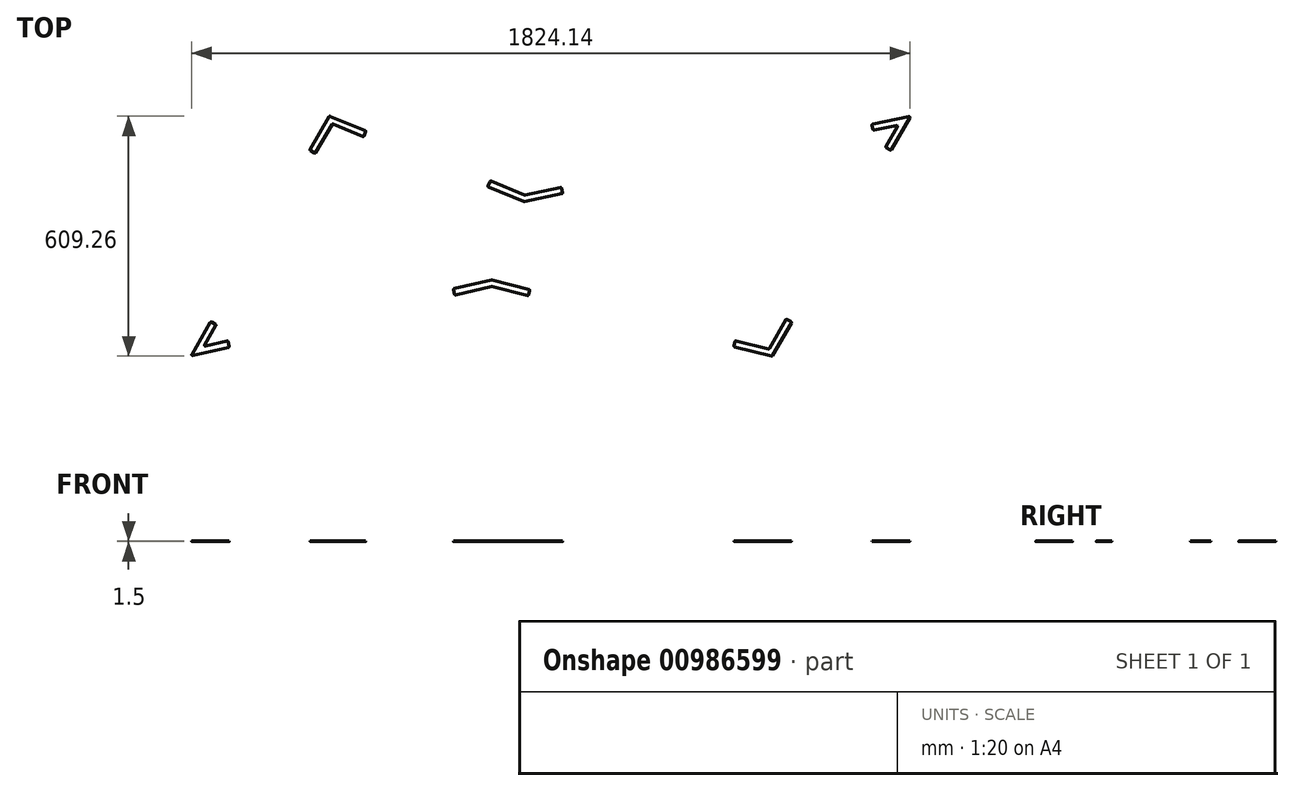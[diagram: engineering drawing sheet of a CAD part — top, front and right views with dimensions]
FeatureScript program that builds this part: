
annotation { "Feature Type Name" : "Feature", "Feature Type Description" : "" }
export const myFeature = defineFeature(function(context is Context, id is Id, definition is map)
    precondition{}
    {
        {
            var Q0;
            Q0=qCreatedBy(makeId("Top.planeOp"),FACE);
            var sketch = newSketch(context, id + "F0", { "sketchPlane" : qUnion([Q0])});
            skLineSegment(sketch, "E0", {"start": v(0, 0) * mm, "end": v(355, 614.88) * mm});
            skLineSegment(sketch, "E1", {"start": v(355, 614.88) * mm, "end": v(851.97, 414.09) * mm});
            skLineSegment(sketch, "E2", {"start": v(355, 614.88) * mm, "end": v(806.95, 614.88) * mm, "construction": true});
            skLineSegment(sketch, "E3", {"start": v(851.97, 414.09) * mm, "end": v(1836.1, 614.88) * mm});
            skLineSegment(sketch, "E4", {"start": v(851.97, 414.09) * mm, "end": v(1531.4, 414.09) * mm, "construction": true});
            skLineSegment(sketch, "E5", {"start": v(1836.1, 614.88) * mm, "end": v(1481.1, 0) * mm});
            skLineSegment(sketch, "E6", {"start": v(1481.1, 0) * mm, "end": v(767.8, 177.26) * mm});
            skLineSegment(sketch, "E7", {"start": v(767.8, 177.26) * mm, "end": v(0, 0) * mm});
            skLineSegment(sketch, "E8.0", {"start": v(767.98, 197.83) * mm, "end": v(40.32, 29.83) * mm});
            skLineSegment(sketch, "E8.1", {"start": v(363.63, 589.82) * mm, "end": v(850.06, 393.29) * mm});
            skLineSegment(sketch, "E8.2", {"start": v(850.06, 393.29) * mm, "end": v(1796.57, 586.4) * mm});
            skLineSegment(sketch, "E8.3", {"start": v(40.32, 29.83) * mm, "end": v(363.63, 589.82) * mm});
            skLineSegment(sketch, "E8.4", {"start": v(1796.57, 586.4) * mm, "end": v(1471.32, 23.04) * mm});
            skLineSegment(sketch, "E8.5", {"start": v(1471.32, 23.04) * mm, "end": v(767.98, 197.83) * mm});
            skLineSegment(sketch, "E9", {"start": v(0, 0) * mm, "end": v(40.32, 29.83) * mm});
            skLineSegment(sketch, "E10", {"start": v(363.63, 589.82) * mm, "end": v(355, 614.88) * mm});
            skLineSegment(sketch, "E11", {"start": v(850.06, 393.29) * mm, "end": v(851.97, 414.09) * mm});
            skLineSegment(sketch, "E12", {"start": v(767.98, 197.83) * mm, "end": v(767.8, 177.26) * mm});
            skLineSegment(sketch, "E13", {"start": v(1471.32, 23.04) * mm, "end": v(1481.1, 0) * mm});
            skLineSegment(sketch, "E14", {"start": v(1796.57, 586.4) * mm, "end": v(1836.1, 614.88) * mm});
            skSolve(sketch);
        }
        {
            var Q0;
            Q0=qCreatedBy(makeId("Top.planeOp"),FACE);
            var sketch = newSketch(context, id + "F1", { "sketchPlane" : qUnion([Q0])});
            skLineSegment(sketch, "E15.0", {"start": v(767.82, 179.32) * mm, "end": v(674.12, 157.69) * mm});
            skLineSegment(sketch, "E15.1", {"start": v(355.86, 612.37) * mm, "end": v(448.58, 574.91) * mm});
            skLineSegment(sketch, "E15.2", {"start": v(851.78, 412) * mm, "end": v(945.04, 431.04) * mm});
            skLineSegment(sketch, "E15.3", {"start": v(4.03, 2.98) * mm, "end": v(54.03, 89.59) * mm});
            skLineSegment(sketch, "E15.4", {"start": v(1832.15, 612.03) * mm, "end": v(1782.15, 525.43) * mm});
            skLineSegment(sketch, "E15.5", {"start": v(1480.13, 2.3) * mm, "end": v(1383.08, 26.42) * mm});
            skLineSegment(sketch, "E16.0", {"start": v(767.96, 195.77) * mm, "end": v(670.52, 173.28) * mm});
            skLineSegment(sketch, "E16.1", {"start": v(362.76, 592.33) * mm, "end": v(442.59, 560.08) * mm});
            skLineSegment(sketch, "E16.2", {"start": v(850.26, 395.37) * mm, "end": v(948.24, 415.36) * mm});
            skLineSegment(sketch, "E16.3", {"start": v(36.29, 26.85) * mm, "end": v(67.89, 81.59) * mm});
            skLineSegment(sketch, "E16.4", {"start": v(1800.53, 589.25) * mm, "end": v(1768.3, 533.43) * mm});
            skLineSegment(sketch, "E16.5", {"start": v(1472.3, 20.74) * mm, "end": v(1386.94, 41.95) * mm});
            skLineSegment(sketch, "E17", {"start": v(67.89, 81.59) * mm, "end": v(54.03, 89.59) * mm});
            skLineSegment(sketch, "E18", {"start": v(97.87, 41.07) * mm, "end": v(101.47, 25.48) * mm});
            skLineSegment(sketch, "E19", {"start": v(319.72, 517.77) * mm, "end": v(305.86, 525.77) * mm});
            skLineSegment(sketch, "E20", {"start": v(442.59, 560.08) * mm, "end": v(448.58, 574.91) * mm});
            skLineSegment(sketch, "E21", {"start": v(758.1, 432.6) * mm, "end": v(764.09, 447.44) * mm});
            skLineSegment(sketch, "E22", {"start": v(948.24, 415.36) * mm, "end": v(945.04, 431.04) * mm});
            skLineSegment(sketch, "E23", {"start": v(1734.17, 592.04) * mm, "end": v(1737.37, 576.36) * mm});
            skLineSegment(sketch, "E24", {"start": v(1768.3, 533.43) * mm, "end": v(1782.15, 525.43) * mm});
            skLineSegment(sketch, "E25", {"start": v(1516.27, 96.9) * mm, "end": v(1530.13, 88.9) * mm});
            skLineSegment(sketch, "E26", {"start": v(1386.94, 41.95) * mm, "end": v(1383.08, 26.42) * mm});
            skLineSegment(sketch, "E27", {"start": v(670.52, 173.28) * mm, "end": v(674.12, 157.69) * mm});
            skLineSegment(sketch, "E28", {"start": v(861.15, 156.13) * mm, "end": v(865, 171.65) * mm});
            skLineSegment(sketch, "E29.trimOffspring", {"start": v(319.72, 517.77) * mm, "end": v(362.76, 592.33) * mm});
            skLineSegment(sketch, "E30.trimOffspring", {"start": v(305.86, 525.77) * mm, "end": v(355.86, 612.37) * mm});
            skLineSegment(sketch, "E31.trimOffspring", {"start": v(758.1, 432.6) * mm, "end": v(850.26, 395.37) * mm});
            skLineSegment(sketch, "E32.trimOffspring", {"start": v(764.09, 447.44) * mm, "end": v(851.78, 412) * mm});
            skLineSegment(sketch, "E33.trimOffspring", {"start": v(1737.37, 576.36) * mm, "end": v(1800.53, 589.25) * mm});
            skLineSegment(sketch, "E34.trimOffspring", {"start": v(1734.17, 592.04) * mm, "end": v(1832.15, 612.03) * mm});
            skLineSegment(sketch, "E35.trimOffspring", {"start": v(1516.27, 96.9) * mm, "end": v(1472.3, 20.74) * mm});
            skLineSegment(sketch, "E36.trimOffspring", {"start": v(1530.13, 88.9) * mm, "end": v(1480.13, 2.3) * mm});
            skLineSegment(sketch, "E37.trimOffspring", {"start": v(865, 171.65) * mm, "end": v(767.96, 195.77) * mm});
            skLineSegment(sketch, "E38.trimOffspring", {"start": v(861.15, 156.13) * mm, "end": v(767.82, 179.32) * mm});
            skLineSegment(sketch, "E39.trimOffspring", {"start": v(101.47, 25.48) * mm, "end": v(4.03, 2.98) * mm});
            skLineSegment(sketch, "E40.trimOffspring", {"start": v(97.87, 41.07) * mm, "end": v(36.29, 26.85) * mm});
            skSolve(sketch);
        }
        {
            var Q0;
            Q0 = qSketchRegion(id + "F1", true);
            extrude(context, id + "F2", {"entities" : qUnion([Q0]), "oppositeDirection" : true, "depth" : 1.5 * mm, "offsetDistance" : 25 * mm});
        }
        {
            var Q0;
            Q0=makeQuery(id+"F2.opExtrude","SWEPT_EDGE",EDGE,{"disambiguationData":[OSD([sQuery(id+"F1.wireOp",EDGE,"E15.1"),sQuery(id+"F1.wireOp",EDGE,"E30.trimOffspring")])]});
            var Q1;
            Q1=makeQuery(id+"F2.opExtrude","SWEPT_EDGE",EDGE,{"disambiguationData":[OSD([sQuery(id+"F1.wireOp",EDGE,"E15.1"),sQuery(id+"F1.wireOp",EDGE,"E20")])]});
            var Q2;
            Q2=makeQuery(id+"F2.opExtrude","SWEPT_EDGE",EDGE,{"disambiguationData":[OSD([sQuery(id+"F1.wireOp",EDGE,"E16.1"),sQuery(id+"F1.wireOp",EDGE,"E20")])]});
            var Q3;
            Q3=makeQuery(id+"F2.opExtrude","SWEPT_EDGE",EDGE,{"disambiguationData":[OSD([sQuery(id+"F1.wireOp",EDGE,"E16.1"),sQuery(id+"F1.wireOp",EDGE,"E29.trimOffspring")])]});
            var Q4;
            Q4=makeQuery(id+"F2.opExtrude","SWEPT_EDGE",EDGE,{"disambiguationData":[OSD([sQuery(id+"F1.wireOp",EDGE,"E19"),sQuery(id+"F1.wireOp",EDGE,"E29.trimOffspring")])]});
            var Q5;
            Q5=makeQuery(id+"F2.opExtrude","SWEPT_EDGE",EDGE,{"disambiguationData":[OSD([sQuery(id+"F1.wireOp",EDGE,"E19"),sQuery(id+"F1.wireOp",EDGE,"E30.trimOffspring")])]});
            fillet(context, id + "F3", {"entities" : qUnion([Q0, Q1, Q2, Q3, Q4, Q5]), "radius" : 2 * mm, "tangentPropagation" : true, "allowEdgeOverflow" : false});
        }
        {
            var Q0;
            Q0=makeQuery(id+"F2.opExtrude","SWEPT_EDGE",EDGE,{"disambiguationData":[OSD([sQuery(id+"F1.wireOp",EDGE,"E21"),sQuery(id+"F1.wireOp",EDGE,"E32.trimOffspring")])]});
            var Q1;
            Q1=makeQuery(id+"F2.opExtrude","SWEPT_EDGE",EDGE,{"disambiguationData":[OSD([sQuery(id+"F1.wireOp",EDGE,"E21"),sQuery(id+"F1.wireOp",EDGE,"E31.trimOffspring")])]});
            var Q2;
            Q2=makeQuery(id+"F2.opExtrude","SWEPT_EDGE",EDGE,{"disambiguationData":[OSD([sQuery(id+"F1.wireOp",EDGE,"E15.2"),sQuery(id+"F1.wireOp",EDGE,"E32.trimOffspring")])]});
            var Q3;
            Q3=makeQuery(id+"F2.opExtrude","SWEPT_EDGE",EDGE,{"disambiguationData":[OSD([sQuery(id+"F1.wireOp",EDGE,"E15.2"),sQuery(id+"F1.wireOp",EDGE,"E22")])]});
            var Q4;
            Q4=makeQuery(id+"F2.opExtrude","SWEPT_EDGE",EDGE,{"disambiguationData":[OSD([sQuery(id+"F1.wireOp",EDGE,"E16.2"),sQuery(id+"F1.wireOp",EDGE,"E22")])]});
            var Q5;
            Q5=makeQuery(id+"F2.opExtrude","SWEPT_EDGE",EDGE,{"disambiguationData":[OSD([sQuery(id+"F1.wireOp",EDGE,"E16.2"),sQuery(id+"F1.wireOp",EDGE,"E31.trimOffspring")])]});
            fillet(context, id + "F4", {"entities" : qUnion([Q0, Q1, Q2, Q3, Q4, Q5]), "radius" : 2 * mm, "tangentPropagation" : true, "allowEdgeOverflow" : false});
        }
        {
            var Q0;
            Q0=makeQuery(id+"F2.opExtrude","SWEPT_EDGE",EDGE,{"disambiguationData":[OSD([sQuery(id+"F1.wireOp",EDGE,"E23"),sQuery(id+"F1.wireOp",EDGE,"E34.trimOffspring")])]});
            var Q1;
            Q1=makeQuery(id+"F2.opExtrude","SWEPT_EDGE",EDGE,{"disambiguationData":[OSD([sQuery(id+"F1.wireOp",EDGE,"E23"),sQuery(id+"F1.wireOp",EDGE,"E33.trimOffspring")])]});
            var Q2;
            Q2=makeQuery(id+"F2.opExtrude","SWEPT_EDGE",EDGE,{"disambiguationData":[OSD([sQuery(id+"F1.wireOp",EDGE,"E16.4"),sQuery(id+"F1.wireOp",EDGE,"E24")])]});
            var Q3;
            Q3=makeQuery(id+"F2.opExtrude","SWEPT_EDGE",EDGE,{"disambiguationData":[OSD([sQuery(id+"F1.wireOp",EDGE,"E15.4"),sQuery(id+"F1.wireOp",EDGE,"E24")])]});
            var Q4;
            Q4=makeQuery(id+"F2.opExtrude","SWEPT_EDGE",EDGE,{"disambiguationData":[OSD([sQuery(id+"F1.wireOp",EDGE,"E16.4"),sQuery(id+"F1.wireOp",EDGE,"E33.trimOffspring")])]});
            var Q5;
            Q5=makeQuery(id+"F2.opExtrude","SWEPT_EDGE",EDGE,{"disambiguationData":[OSD([sQuery(id+"F1.wireOp",EDGE,"E15.4"),sQuery(id+"F1.wireOp",EDGE,"E34.trimOffspring")])]});
            fillet(context, id + "F5", {"entities" : qUnion([Q0, Q1, Q2, Q3, Q4, Q5]), "radius" : 2 * mm, "tangentPropagation" : true, "allowEdgeOverflow" : false});
        }
        {
            var Q0;
            Q0=makeQuery(id+"F2.opExtrude","SWEPT_EDGE",EDGE,{"disambiguationData":[OSD([sQuery(id+"F1.wireOp",EDGE,"E16.5"),sQuery(id+"F1.wireOp",EDGE,"E26")])]});
            var Q1;
            Q1=makeQuery(id+"F2.opExtrude","SWEPT_EDGE",EDGE,{"disambiguationData":[OSD([sQuery(id+"F1.wireOp",EDGE,"E15.5"),sQuery(id+"F1.wireOp",EDGE,"E26")])]});
            var Q2;
            Q2=makeQuery(id+"F2.opExtrude","SWEPT_EDGE",EDGE,{"disambiguationData":[OSD([sQuery(id+"F1.wireOp",EDGE,"E16.5"),sQuery(id+"F1.wireOp",EDGE,"E35.trimOffspring")])]});
            var Q3;
            Q3=makeQuery(id+"F2.opExtrude","SWEPT_EDGE",EDGE,{"disambiguationData":[OSD([sQuery(id+"F1.wireOp",EDGE,"E15.5"),sQuery(id+"F1.wireOp",EDGE,"E36.trimOffspring")])]});
            var Q4;
            Q4=makeQuery(id+"F2.opExtrude","SWEPT_EDGE",EDGE,{"disambiguationData":[OSD([sQuery(id+"F1.wireOp",EDGE,"E25"),sQuery(id+"F1.wireOp",EDGE,"E35.trimOffspring")])]});
            var Q5;
            Q5=makeQuery(id+"F2.opExtrude","SWEPT_EDGE",EDGE,{"disambiguationData":[OSD([sQuery(id+"F1.wireOp",EDGE,"E25"),sQuery(id+"F1.wireOp",EDGE,"E36.trimOffspring")])]});
            fillet(context, id + "F6", {"entities" : qUnion([Q0, Q1, Q2, Q3, Q4, Q5]), "radius" : 2 * mm, "tangentPropagation" : true, "allowEdgeOverflow" : false});
        }
        {
            var Q0;
            Q0=makeQuery(id+"F2.opExtrude","SWEPT_EDGE",EDGE,{"disambiguationData":[OSD([sQuery(id+"F1.wireOp",EDGE,"E15.0"),sQuery(id+"F1.wireOp",EDGE,"E27")])]});
            var Q1;
            Q1=makeQuery(id+"F2.opExtrude","SWEPT_EDGE",EDGE,{"disambiguationData":[OSD([sQuery(id+"F1.wireOp",EDGE,"E16.0"),sQuery(id+"F1.wireOp",EDGE,"E27")])]});
            var Q2;
            Q2=makeQuery(id+"F2.opExtrude","SWEPT_EDGE",EDGE,{"disambiguationData":[OSD([sQuery(id+"F1.wireOp",EDGE,"E15.0"),sQuery(id+"F1.wireOp",EDGE,"E38.trimOffspring")])]});
            var Q3;
            Q3=makeQuery(id+"F2.opExtrude","SWEPT_EDGE",EDGE,{"disambiguationData":[OSD([sQuery(id+"F1.wireOp",EDGE,"E28"),sQuery(id+"F1.wireOp",EDGE,"E38.trimOffspring")])]});
            var Q4;
            Q4=makeQuery(id+"F2.opExtrude","SWEPT_EDGE",EDGE,{"disambiguationData":[OSD([sQuery(id+"F1.wireOp",EDGE,"E28"),sQuery(id+"F1.wireOp",EDGE,"E37.trimOffspring")])]});
            var Q5;
            Q5=makeQuery(id+"F2.opExtrude","SWEPT_EDGE",EDGE,{"disambiguationData":[OSD([sQuery(id+"F1.wireOp",EDGE,"E16.0"),sQuery(id+"F1.wireOp",EDGE,"E37.trimOffspring")])]});
            fillet(context, id + "F7", {"entities" : qUnion([Q0, Q1, Q2, Q3, Q4, Q5]), "radius" : 2 * mm, "tangentPropagation" : true, "allowEdgeOverflow" : false});
        }
        {
            var Q0;
            Q0=makeQuery(id+"F2.opExtrude","SWEPT_EDGE",EDGE,{"disambiguationData":[OSD([sQuery(id+"F1.wireOp",EDGE,"E18"),sQuery(id+"F1.wireOp",EDGE,"E39.trimOffspring")])]});
            var Q1;
            Q1=makeQuery(id+"F2.opExtrude","SWEPT_EDGE",EDGE,{"disambiguationData":[OSD([sQuery(id+"F1.wireOp",EDGE,"E18"),sQuery(id+"F1.wireOp",EDGE,"E40.trimOffspring")])]});
            var Q2;
            Q2=makeQuery(id+"F2.opExtrude","SWEPT_EDGE",EDGE,{"disambiguationData":[OSD([sQuery(id+"F1.wireOp",EDGE,"E15.3"),sQuery(id+"F1.wireOp",EDGE,"E39.trimOffspring")])]});
            var Q3;
            Q3=makeQuery(id+"F2.opExtrude","SWEPT_EDGE",EDGE,{"disambiguationData":[OSD([sQuery(id+"F1.wireOp",EDGE,"E15.3"),sQuery(id+"F1.wireOp",EDGE,"E17")])]});
            var Q4;
            Q4=makeQuery(id+"F2.opExtrude","SWEPT_EDGE",EDGE,{"disambiguationData":[OSD([sQuery(id+"F1.wireOp",EDGE,"E16.3"),sQuery(id+"F1.wireOp",EDGE,"E17")])]});
            var Q5;
            Q5=makeQuery(id+"F2.opExtrude","SWEPT_EDGE",EDGE,{"disambiguationData":[OSD([sQuery(id+"F1.wireOp",EDGE,"E16.3"),sQuery(id+"F1.wireOp",EDGE,"E40.trimOffspring")])]});
            fillet(context, id + "F8", {"entities" : qUnion([Q0, Q1, Q2, Q3, Q4, Q5]), "radius" : 2 * mm, "tangentPropagation" : true, "allowEdgeOverflow" : false});
        }
    });
